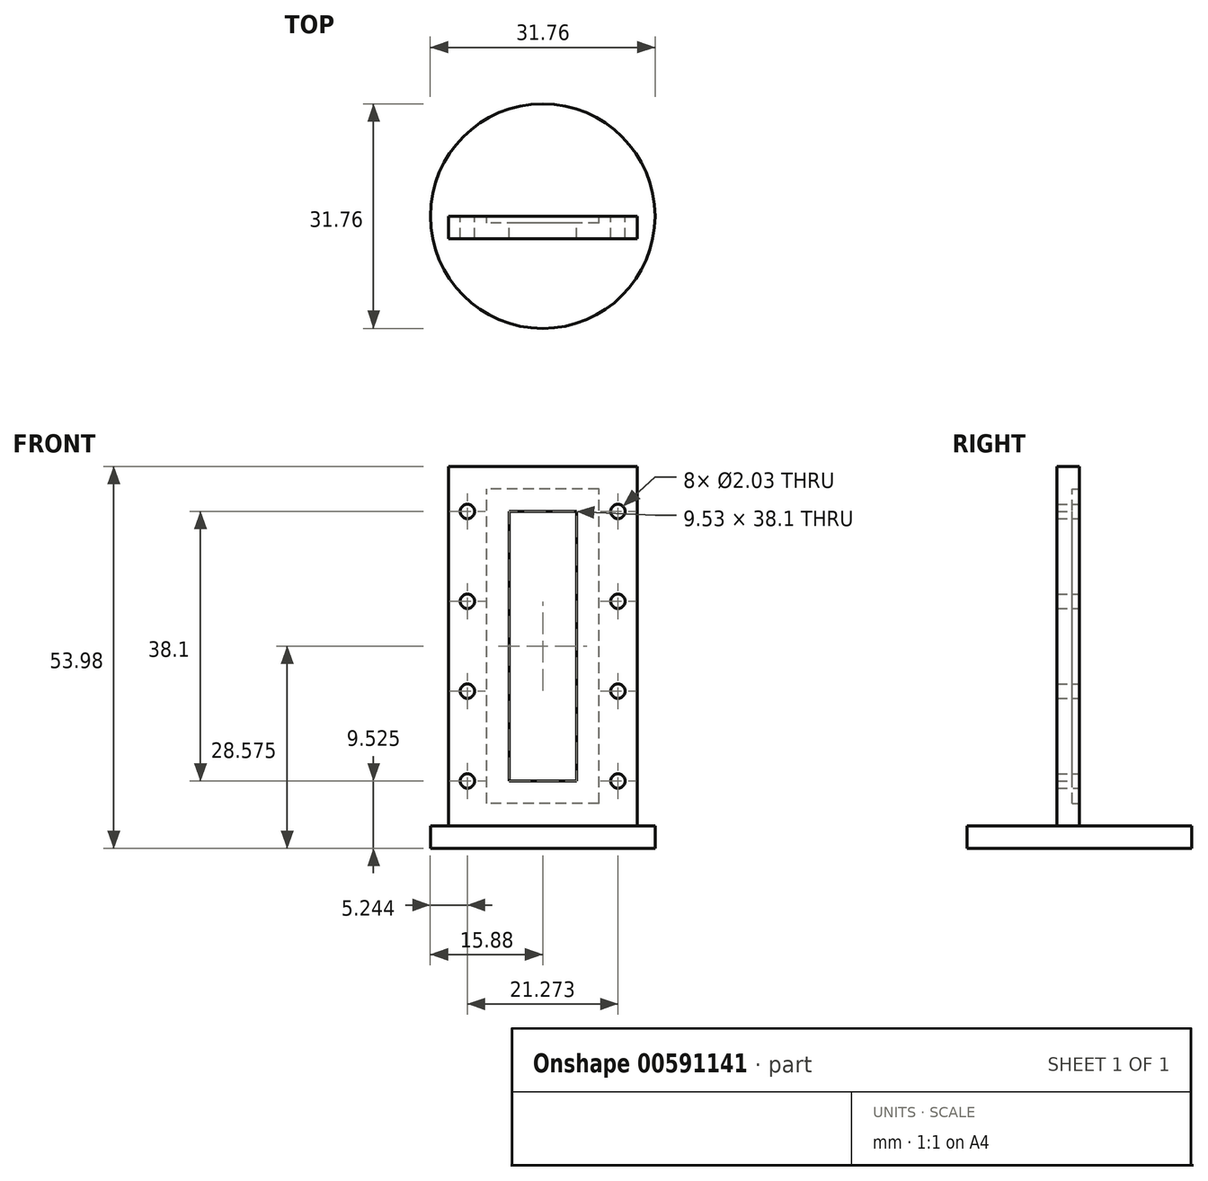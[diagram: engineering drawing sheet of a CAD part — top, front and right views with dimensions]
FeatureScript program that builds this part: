
annotation { "Feature Type Name" : "Feature", "Feature Type Description" : "" }
export const myFeature = defineFeature(function(context is Context, id is Id, definition is map)
    precondition{}
    {
        {
            var Q0;
            Q0=qCreatedBy(makeId("Top.planeOp"),FACE);
            var sketch = newSketch(context, id + "F0", { "sketchPlane" : qUnion([Q0])});
            skCircle(sketch, "E0", {"center": v(0, 0) * mm, "radius": 15.88 * mm});
            skSolve(sketch);
        }
        {
            var Q0;
            Q0=makeQuery(id+"F0.imprint","IMPRINT",FACE,{"disambiguationData":[TD([[makeQuery(id+"F0.imprint","IMPRINT",EDGE,{"derivedFrom":sQuery(id+"F0.wireOp",EDGE,"E0")}),1.0]])]});
            extrude(context, id + "F1", {"entities" : qUnion([Q0]), "depth" : 3.17 * mm, "offsetDistance" : 25.4 * mm});
        }
        {
            var Q0;
            Q0=makeQuery(id+"F1.opExtrude","CAP_FACE",FACE,{"disambiguationData":[OSD([sQuery(id+"F0.wireOp",EDGE,"E0")])],"isStart":false});
            var sketch = newSketch(context, id + "F2", { "sketchPlane" : qUnion([Q0])});
            skLineSegment(sketch, "E1.bottom", {"start": v(-13.33, 0) * mm, "end": v(13.33, 0) * mm});
            skLineSegment(sketch, "E1.top", {"start": v(-13.33, -3.17) * mm, "end": v(13.33, -3.17) * mm});
            skLineSegment(sketch, "E1.left", {"start": v(-13.33, 0) * mm, "end": v(-13.33, -3.18) * mm});
            skLineSegment(sketch, "E1.right", {"start": v(13.33, 0) * mm, "end": v(13.33, -3.17) * mm});
            skSolve(sketch);
        }
        {
            var Q0;
            Q0=makeQuery(id+"F2.imprint","IMPRINT",FACE,{"disambiguationData":[TD([[makeQuery(id+"F2.imprint","IMPRINT",EDGE,{"derivedFrom":sQuery(id+"F2.wireOp",EDGE,"E1.bottom")}),-1.0]])]});
            extrude(context, id + "F3", {"entities" : qUnion([Q0]), "operationType" : NewBodyOperationType.ADD, "depth" : 50.8 * mm, "offsetDistance" : 25.4 * mm});
        }
        {
            var Q0;
            Q0=makeQuery(id+"F3.opExtrude","SWEPT_FACE",FACE,{"disambiguationData":[OSD([sQuery(id+"F2.wireOp",EDGE,"E1.bottom")])]});
            var sketch = newSketch(context, id + "F4", { "sketchPlane" : qUnion([Q0])});
            skLineSegment(sketch, "E2.bottom", {"start": v(-4.76, 9.53) * mm, "end": v(4.76, 9.53) * mm});
            skLineSegment(sketch, "E2.top", {"start": v(-4.76, 47.62) * mm, "end": v(4.76, 47.62) * mm});
            skLineSegment(sketch, "E2.left", {"start": v(-4.76, 9.52) * mm, "end": v(-4.76, 47.62) * mm});
            skLineSegment(sketch, "E2.right", {"start": v(4.76, 9.53) * mm, "end": v(4.76, 47.62) * mm});
            skLineSegment(sketch, "E3", {"start": v(0, 3.18) * mm, "end": v(0, 53.98) * mm, "construction": true});
            skPoint(sketch, "E4", {"position": v(0, 47.62) * mm});
            skSolve(sketch);
        }
        {
            var Q0;
            Q0=makeQuery(id+"F4.imprint","IMPRINT",FACE,{"disambiguationData":[TD([[makeQuery(id+"F4.imprint","IMPRINT",EDGE,{"derivedFrom":sQuery(id+"F4.wireOp",EDGE,"E2.bottom")}),1.0]])]});
            extrude(context, id + "F5", {"entities" : qUnion([Q0]), "operationType" : NewBodyOperationType.REMOVE, "endBound" : BoundingType.UP_TO_NEXT, "oppositeDirection" : true, "depth" : 25.4 * mm, "offsetDistance" : 25.4 * mm});
        }
        {
            var Q0;
            Q0=makeQuery(id+"F3.opExtrude","SWEPT_FACE",FACE,{"disambiguationData":[OSD([sQuery(id+"F2.wireOp",EDGE,"E1.bottom")])]});
            var sketch = newSketch(context, id + "F6", { "sketchPlane" : qUnion([Q0])});
            skLineSegment(sketch, "E5.0", {"start": v(7.94, 6.35) * mm, "end": v(7.94, 50.8) * mm});
            skLineSegment(sketch, "E5.1", {"start": v(-7.94, 6.35) * mm, "end": v(7.94, 6.35) * mm});
            skLineSegment(sketch, "E5.2", {"start": v(-7.94, 6.35) * mm, "end": v(-7.94, 50.8) * mm});
            skLineSegment(sketch, "E5.3", {"start": v(-7.94, 50.8) * mm, "end": v(7.94, 50.8) * mm});
            skSolve(sketch);
        }
        {
            var Q0;
            Q0=makeQuery(id+"F6.imprint","IMPRINT",FACE,{"disambiguationData":[TD([[makeQuery(id+"F6.imprint","IMPRINT",EDGE,{"derivedFrom":sQuery(id+"F6.wireOp",EDGE,"E5.0")}),1.0]])]});
            extrude(context, id + "F7", {"entities" : qUnion([Q0]), "operationType" : NewBodyOperationType.REMOVE, "oppositeDirection" : true, "depth" : 1 * mm, "offsetDistance" : 25.4 * mm});
        }
        {
            var Q0;
            Q0=makeQuery(id+"F3.opExtrude","SWEPT_FACE",FACE,{"disambiguationData":[OSD([sQuery(id+"F2.wireOp",EDGE,"E1.bottom")])]});
            var sketch = newSketch(context, id + "F8", { "sketchPlane" : qUnion([Q0])});
            skCircle(sketch, "E6", {"center": v(10.64, 9.53) * mm, "radius": 1.02 * mm});
            skLineSegment(sketch, "E7", {"start": v(10.64, 9.53) * mm, "end": v(7.94, 9.53) * mm});
            skLineSegment(sketch, "E8", {"start": v(10.64, 9.53) * mm, "end": v(13.33, 9.53) * mm});
            skCircle(sketch, "E9.0.1.0", {"center": v(10.64, 22.22) * mm, "radius": 1.02 * mm});
            skCircle(sketch, "E9.0.2.0", {"center": v(10.64, 34.92) * mm, "radius": 1.02 * mm});
            skCircle(sketch, "E9.0.3.0", {"center": v(10.64, 47.62) * mm, "radius": 1.02 * mm});
            skLineSegment(sketch, "E9.direction1", {"start": v(10.64, 9.53) * mm, "end": v(-14.76, 9.52) * mm, "construction": true});
            skLineSegment(sketch, "E9.direction2", {"start": v(10.64, 9.53) * mm, "end": v(10.64, 22.22) * mm, "construction": true});
            skCircle(sketch, "E10.MirrorC", {"center": v(-10.64, 47.62) * mm, "radius": 1.02 * mm});
            skCircle(sketch, "E11.MirrorC", {"center": v(-10.64, 34.92) * mm, "radius": 1.02 * mm});
            skCircle(sketch, "E12.MirrorC", {"center": v(-10.64, 22.22) * mm, "radius": 1.02 * mm});
            skCircle(sketch, "E13.MirrorC", {"center": v(-10.64, 9.53) * mm, "radius": 1.02 * mm});
            skSolve(sketch);
        }
        {
            var Q0;
            Q0 = qSketchRegion(id + "F8", true);
            extrude(context, id + "F9", {"entities" : qUnion([Q0]), "operationType" : NewBodyOperationType.REMOVE, "endBound" : BoundingType.UP_TO_NEXT, "oppositeDirection" : true, "depth" : 25.4 * mm, "offsetDistance" : 25.4 * mm});
        }
    });
